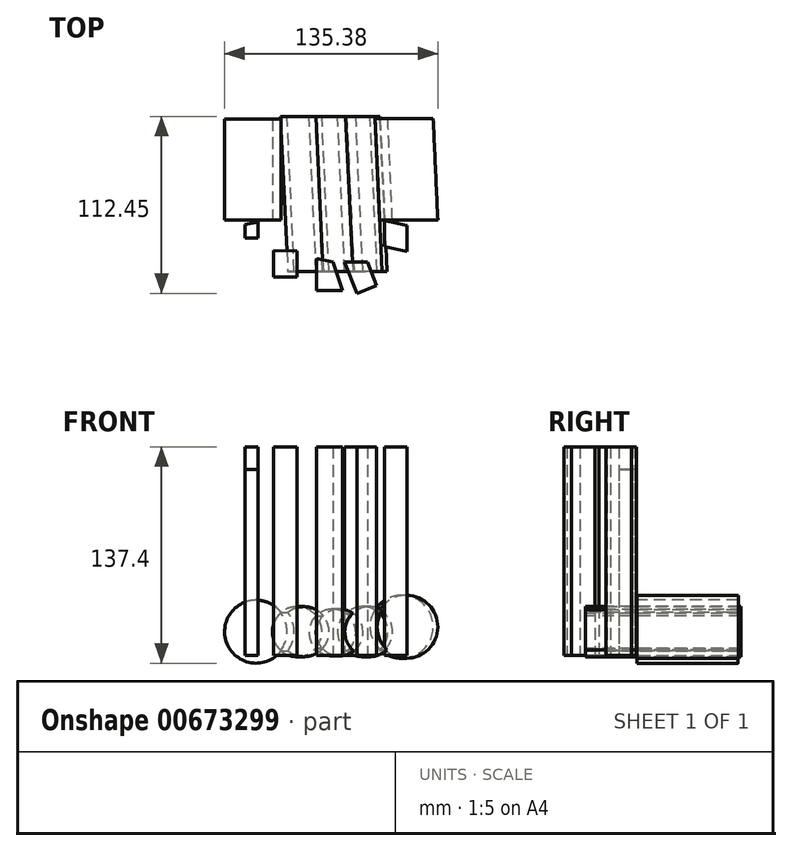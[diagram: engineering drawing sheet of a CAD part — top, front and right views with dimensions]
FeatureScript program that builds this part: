
annotation { "Feature Type Name" : "Feature", "Feature Type Description" : "" }
export const myFeature = defineFeature(function(context is Context, id is Id, definition is map)
    precondition{}
    {
        {
            var Q0;
            Q0=qCreatedBy(makeId("Front.planeOp"),FACE);
            var sketch = newSketch(context, id + "F0", { "sketchPlane" : qUnion([Q0])});
            skCircle(sketch, "E0", {"center": v(0, 14.69) * mm, "radius": 14.84 * mm});
            skCircle(sketch, "E1", {"center": v(19.2, 15.2) * mm, "radius": 15.9 * mm});
            skCircle(sketch, "E2", {"center": v(43.9, 18.29) * mm, "radius": 20.01 * mm});
            skCircle(sketch, "E3", {"center": v(-22.58, 15.2) * mm, "radius": 15.9 * mm});
            skCircle(sketch, "E4", {"center": v(-48.83, 15.2) * mm, "radius": 20.01 * mm});
            skSolve(sketch);
        }
        {
            var Q0;
            Q0=qCreatedBy(makeId("Top.planeOp"),FACE);
            var sketch = newSketch(context, id + "F1", { "sketchPlane" : qUnion([Q0])});
            skLineSegment(sketch, "E5", {"start": v(-44.02, 6.72) * mm, "end": v(-44.02, -57.38) * mm});
            skLineSegment(sketch, "E6", {"start": v(-30.74, 8.43) * mm, "end": v(-26.22, -90.12) * mm});
            skLineSegment(sketch, "E7", {"start": v(-10.56, 4.9) * mm, "end": v(-6.2, -90.12) * mm});
            skLineSegment(sketch, "E8", {"start": v(9.51, 7.45) * mm, "end": v(14, -90.12) * mm});
            skLineSegment(sketch, "E9", {"start": v(32.67, 6.9) * mm, "end": v(35.62, -57.38) * mm});
            skSolve(sketch);
        }
        {
            var Q0;
            {var subQ0=sQuery(id+"F0.wireOp",EDGE,"E4");var subQ1=sQuery(id+"F0.wireOp",EDGE,"E3");var subQ2=makeQuery(id+"F0.imprint","INTERSECT",VERTEX,{"disambiguationData":[OD(0.0)],"derivedFrom":[subQ1,subQ0]});Q0=makeQuery(id+"F0.imprint","IMPRINT",FACE,{"disambiguationData":[TD([[makeQuery(id+"F0.imprint","IMPRINT",EDGE,{"disambiguationData":[TD([[subQ2,-1.0]])],"derivedFrom":subQ1}),-1.0]])]});}
            var Q1;
            Q1=sQuery(id+"F1.wireOp",EDGE,"E5");
            sweep(context, id + "F2", {"profiles" : qUnion([Q0]), "path" : qUnion([Q1])});
        }
        {
            var Q0;
            {var subQ0=sQuery(id+"F0.wireOp",EDGE,"E3");var subQ1=sQuery(id+"F0.wireOp",EDGE,"E0");var subQ2=makeQuery(id+"F0.imprint","INTERSECT",VERTEX,{"disambiguationData":[OD(0.0)],"derivedFrom":[subQ1,subQ0]});Q0=makeQuery(id+"F0.imprint","IMPRINT",FACE,{"disambiguationData":[TD([[makeQuery(id+"F0.imprint","IMPRINT",EDGE,{"disambiguationData":[TD([[subQ2,-1.0]])],"derivedFrom":subQ1}),-1.0]])]});}
            var Q1;
            {var subQ0=sQuery(id+"F0.wireOp",EDGE,"E3");var subQ1=sQuery(id+"F0.wireOp",EDGE,"E0");var subQ2=makeQuery(id+"F0.imprint","INTERSECT",VERTEX,{"disambiguationData":[OD(0.0)],"derivedFrom":[subQ1,subQ0]});Q1=makeQuery(id+"F0.imprint","IMPRINT",FACE,{"disambiguationData":[TD([[makeQuery(id+"F0.imprint","IMPRINT",EDGE,{"disambiguationData":[TD([[subQ2,1.0]])],"derivedFrom":subQ1}),1.0]])]});}
            var Q2;
            {var subQ0=sQuery(id+"F0.wireOp",EDGE,"E1");var subQ1=sQuery(id+"F0.wireOp",EDGE,"E0");var subQ2=makeQuery(id+"F0.imprint","INTERSECT",VERTEX,{"disambiguationData":[OD(0.0)],"derivedFrom":[subQ1,subQ0]});Q2=makeQuery(id+"F0.imprint","IMPRINT",FACE,{"disambiguationData":[TD([[makeQuery(id+"F0.imprint","IMPRINT",EDGE,{"disambiguationData":[TD([[subQ2,1.0]])],"derivedFrom":subQ1}),-1.0]])]});}
            var Q3;
            Q3=sQuery(id+"F1.wireOp",EDGE,"E6");
            sweep(context, id + "F3", {"operationType" : NewBodyOperationType.ADD, "profiles" : qUnion([Q0, Q1, Q2]), "path" : qUnion([Q3])});
        }
        {
            var Q0;
            {var subQ0=sQuery(id+"F0.wireOp",EDGE,"E2");var subQ1=sQuery(id+"F0.wireOp",EDGE,"E1");var subQ2=makeQuery(id+"F0.imprint","INTERSECT",VERTEX,{"disambiguationData":[OD(0.0)],"derivedFrom":[subQ1,subQ0]});Q0=makeQuery(id+"F0.imprint","IMPRINT",FACE,{"disambiguationData":[TD([[makeQuery(id+"F0.imprint","IMPRINT",EDGE,{"disambiguationData":[TD([[subQ2,1.0]])],"derivedFrom":subQ1}),-1.0]])]});}
            var Q1;
            Q1=sQuery(id+"F1.wireOp",EDGE,"E9");
            sweep(context, id + "F4", {"operationType" : NewBodyOperationType.ADD, "profiles" : qUnion([Q0]), "path" : qUnion([Q1]), "keepProfileOrientation" : true});
        }
        {
            var Q0;
            Q0=qCreatedBy(makeId("Top.planeOp"),FACE);
            var sketch = newSketch(context, id + "F5", { "sketchPlane" : qUnion([Q0])});
            skLineSegment(sketch, "E10", {"start": v(-55.94, -60.43) * mm, "end": v(-55.94, -69) * mm});
            skLineSegment(sketch, "E11", {"start": v(-55.94, -69) * mm, "end": v(-47.54, -69) * mm});
            skLineSegment(sketch, "E12", {"start": v(-47.54, -69) * mm, "end": v(-47.54, -58.66) * mm});
            skLineSegment(sketch, "E13", {"start": v(-47.54, -58.66) * mm, "end": v(-55.94, -60.43) * mm});
            skLineSegment(sketch, "E14", {"start": v(-37.7, -76.7) * mm, "end": v(-37.7, -93.8) * mm});
            skLineSegment(sketch, "E15", {"start": v(-37.7, -93.8) * mm, "end": v(-22.93, -93.8) * mm});
            skLineSegment(sketch, "E16", {"start": v(-22.93, -93.8) * mm, "end": v(-22.93, -77.26) * mm});
            skLineSegment(sketch, "E17", {"start": v(-22.93, -77.26) * mm, "end": v(-37.7, -76.7) * mm});
            skLineSegment(sketch, "E18", {"start": v(-10.5, -81.8) * mm, "end": v(-10.5, -102.07) * mm});
            skLineSegment(sketch, "E19", {"start": v(-10.5, -102.07) * mm, "end": v(6.08, -102.07) * mm});
            skLineSegment(sketch, "E20", {"start": v(6.08, -102.07) * mm, "end": v(0, -84.15) * mm});
            skLineSegment(sketch, "E21", {"start": v(0, -84.15) * mm, "end": v(-10.5, -81.8) * mm});
            skLineSegment(sketch, "E22", {"start": v(7.38, -84.15) * mm, "end": v(15.17, -104.02) * mm});
            skLineSegment(sketch, "E23", {"start": v(15.17, -104.02) * mm, "end": v(27.7, -99.1) * mm});
            skLineSegment(sketch, "E24", {"start": v(27.7, -99.1) * mm, "end": v(21.84, -84.15) * mm});
            skLineSegment(sketch, "E25", {"start": v(21.84, -84.15) * mm, "end": v(7.38, -84.15) * mm});
            skLineSegment(sketch, "E26", {"start": v(46.9, -50.75) * mm, "end": v(46.9, -77.36) * mm});
            skLineSegment(sketch, "E27", {"start": v(46.9, -77.36) * mm, "end": v(32.83, -74.22) * mm});
            skLineSegment(sketch, "E28", {"start": v(32.83, -74.22) * mm, "end": v(32.83, -57.87) * mm});
            skLineSegment(sketch, "E29", {"start": v(32.83, -57.87) * mm, "end": v(46.9, -61.01) * mm});
            skSolve(sketch);
        }
        {
            var Q0;
            Q0=makeQuery(id+"F5.imprint","IMPRINT",FACE,{"disambiguationData":[TD([[makeQuery(id+"F5.imprint","IMPRINT",EDGE,{"derivedFrom":sQuery(id+"F5.wireOp",EDGE,"E10")}),1.0]])]});
            extrude(context, id + "F6", {"entities" : qUnion([Q0]), "depth" : 118.36 * mm, "offsetDistance" : 25.4 * mm});
        }
        {
            var Q0;
            Q0 = qSketchRegion(id + "F5", true);
            extrude(context, id + "F7", {"entities" : qUnion([Q0]), "depth" : 132.6 * mm, "offsetDistance" : 25.4 * mm});
        }
    });
